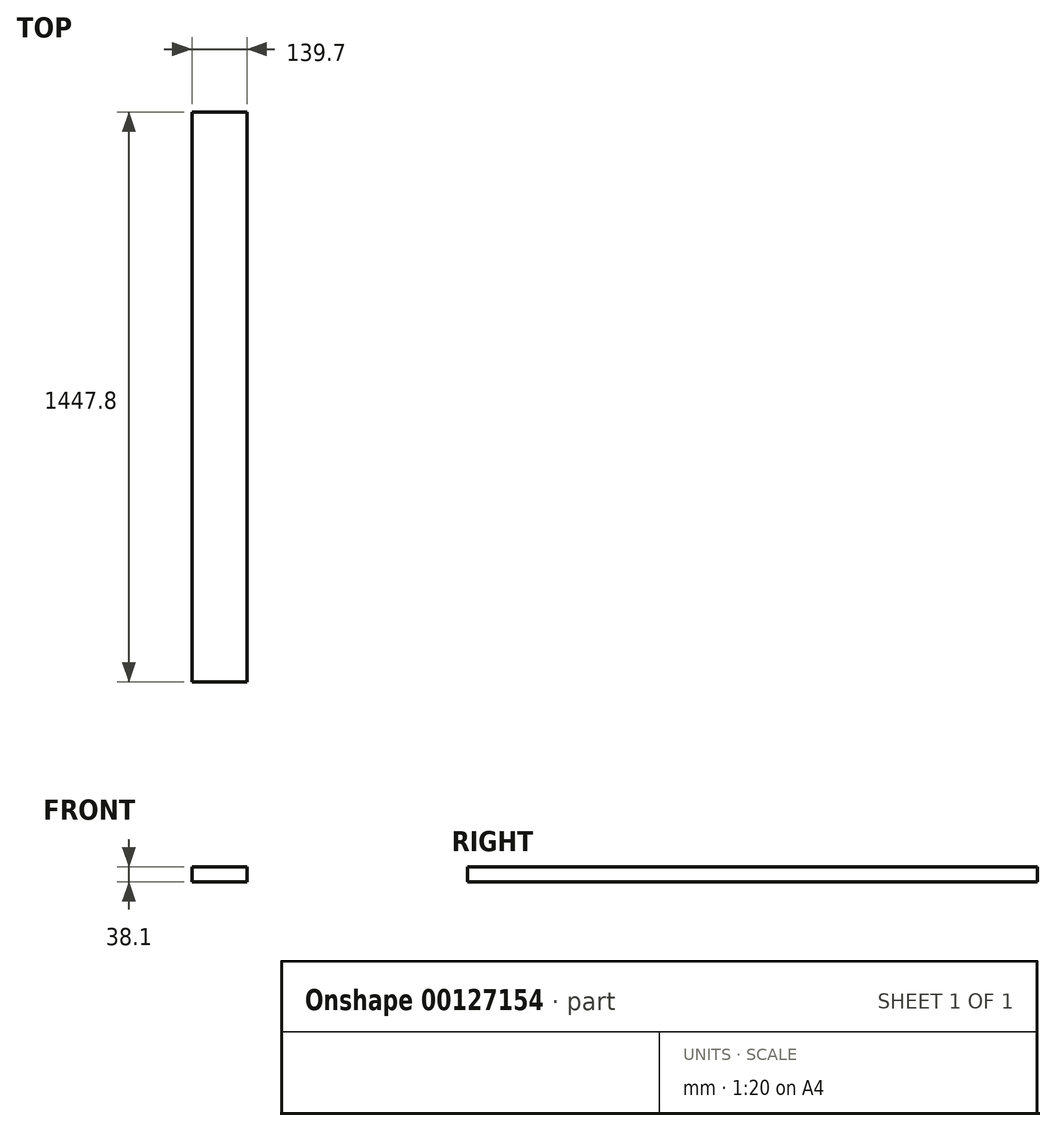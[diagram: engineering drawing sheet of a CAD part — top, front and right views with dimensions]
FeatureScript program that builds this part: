
annotation { "Feature Type Name" : "Feature", "Feature Type Description" : "" }
export const myFeature = defineFeature(function(context is Context, id is Id, definition is map)
    precondition{}
    {
        {
            var Q0;
            Q0=qCreatedBy(makeId("Front.planeOp"),FACE);
            var sketch = newSketch(context, id + "F0", { "sketchPlane" : qUnion([Q0])});
            skLineSegment(sketch, "E0.bottom", {"start": v(69.85, -19.05) * mm, "end": v(-69.85, -19.05) * mm});
            skLineSegment(sketch, "E0.top", {"start": v(69.85, 19.05) * mm, "end": v(-69.85, 19.05) * mm});
            skLineSegment(sketch, "E0.left", {"start": v(69.85, -19.05) * mm, "end": v(69.85, 19.05) * mm});
            skLineSegment(sketch, "E0.right", {"start": v(-69.85, -19.05) * mm, "end": v(-69.85, 19.05) * mm});
            skPoint(sketch, "E0.middle", {"position": v(0, 0) * mm});
            skSolve(sketch);
        }
        {
            var Q0;
            Q0=qSketchRegion(id+"F0",true);
            extrude(context, id + "F1", {"entities" : qUnion([Q0]), "depth" : 1447.8 * mm, "offsetDistance" : 25.4 * mm});
        }
    });
